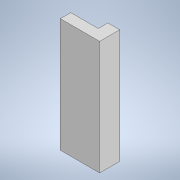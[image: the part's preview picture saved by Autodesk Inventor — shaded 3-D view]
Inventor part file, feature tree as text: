
AUTODESK INVENTOR PART (.ipt)
format: ipt  version: 2020.1 (Build 241239000, 239)  size: 96,256 bytes
history: native  units: mm
features: other x1, extrude x1, sketch x1
ambient origin geometry x8: Origin, YZ Plane, XZ Plane, XY Plane, X Axis, Y Axis, Z Axis, Center Point
bodies: Body1 (feature_tree)
feature tree (3):
  other  "Твердое тело1"
  extrude  "Выдавливание1"  Depth=26.5mm
  sketch  "Эскиз1"
